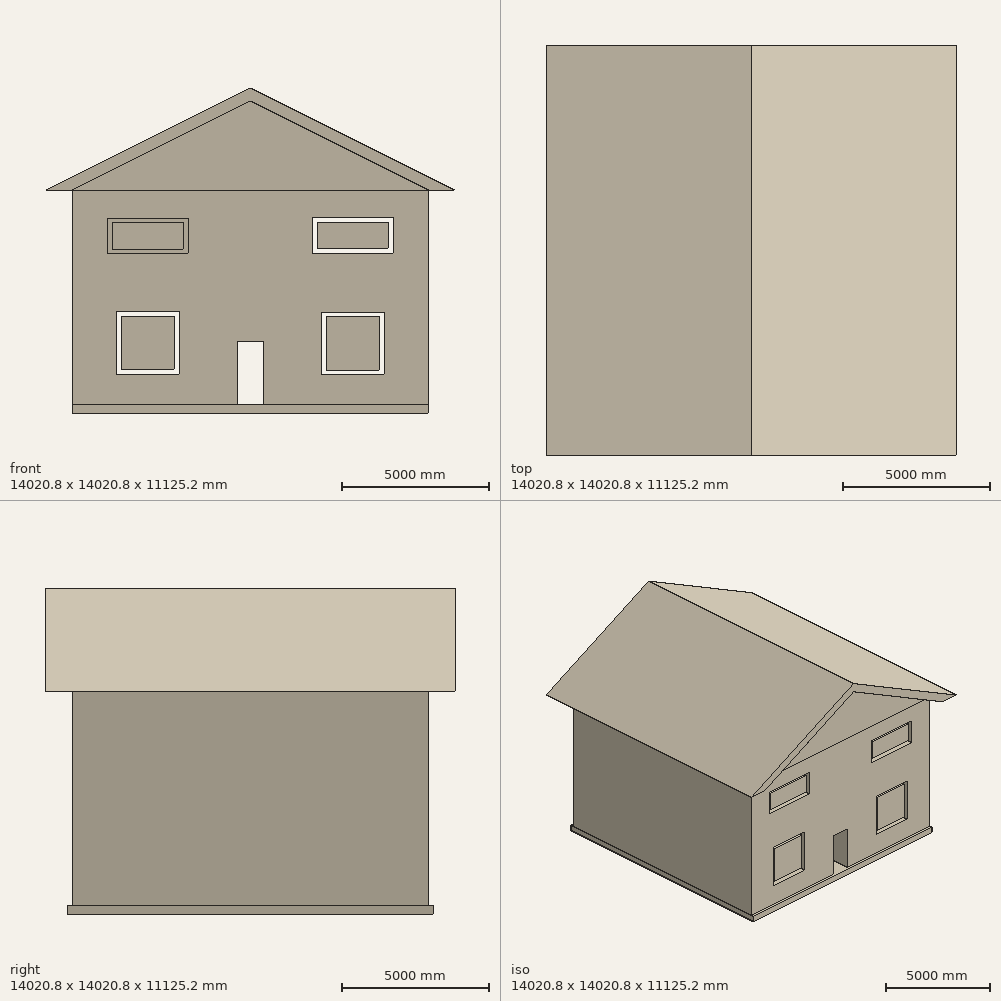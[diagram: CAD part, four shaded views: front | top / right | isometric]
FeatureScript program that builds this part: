
annotation { "Feature Type Name" : "Feature", "Feature Type Description" : "" }
export const myFeature = defineFeature(function(context is Context, id is Id, definition is map)
    precondition{}
    {
        {
            var Q0;
            Q0=qCreatedBy(makeId("Front.planeOp"),FACE);
            var sketch = newSketch(context, id + "F0", { "sketchPlane" : qUnion([Q0])});
            skLineSegment(sketch, "E0", {"start": v(0, 0) * mm, "end": v(-6096, 0) * mm});
            skLineSegment(sketch, "E1", {"start": v(0, 0) * mm, "end": v(6096, 0) * mm});
            skLineSegment(sketch, "E2", {"start": v(0, 0) * mm, "end": v(0, 3048) * mm, "construction": true});
            skLineSegment(sketch, "E3", {"start": v(-6096, 0) * mm, "end": v(0, 3048) * mm});
            skLineSegment(sketch, "E4", {"start": v(0, 3048) * mm, "end": v(6096, 0) * mm});
            skLineSegment(sketch, "E5", {"start": v(-6096, 0) * mm, "end": v(-7010.4, 0) * mm});
            skLineSegment(sketch, "E6", {"start": v(6096, 0) * mm, "end": v(7010.4, 0) * mm});
            skLineSegment(sketch, "E7", {"start": v(0, 3048) * mm, "end": v(0, 3505.2) * mm});
            skLineSegment(sketch, "E8", {"start": v(0, 3505.2) * mm, "end": v(7010.4, 0) * mm});
            skLineSegment(sketch, "E9", {"start": v(-7010.4, 0) * mm, "end": v(0, 3505.2) * mm});
            skLineSegment(sketch, "E10", {"start": v(-6096, 0) * mm, "end": v(-6096, -7315.2) * mm});
            skLineSegment(sketch, "E11", {"start": v(6096, 0) * mm, "end": v(6096, -7315.2) * mm});
            skLineSegment(sketch, "E12", {"start": v(-6096, -7315.2) * mm, "end": v(6096, -7315.2) * mm});
            skLineSegment(sketch, "E13", {"start": v(-6096, -7315.2) * mm, "end": v(-6096, -7620) * mm});
            skLineSegment(sketch, "E14", {"start": v(-6096, -7620) * mm, "end": v(6096, -7620) * mm});
            skLineSegment(sketch, "E15", {"start": v(6096, -7620) * mm, "end": v(6096, -7315.2) * mm});
            skLineSegment(sketch, "E16", {"start": v(0, 0) * mm, "end": v(0, -7315.2) * mm, "construction": true});
            skLineSegment(sketch, "E17", {"start": v(0, -7315.2) * mm, "end": v(-457.2, -7315.2) * mm});
            skLineSegment(sketch, "E18", {"start": v(-457.2, -7315.2) * mm, "end": v(-457.2, -5181.6) * mm});
            skLineSegment(sketch, "E19", {"start": v(-457.2, -5181.6) * mm, "end": v(457.2, -5181.6) * mm});
            skLineSegment(sketch, "E20", {"start": v(457.2, -5181.6) * mm, "end": v(457.2, -7315.2) * mm});
            skLineSegment(sketch, "E21", {"start": v(457.2, -7315.2) * mm, "end": v(0, -7315.2) * mm});
            skLineSegment(sketch, "E22.bottom", {"start": v(2438.4, -4174.44) * mm, "end": v(4572, -4174.44) * mm});
            skLineSegment(sketch, "E22.top", {"start": v(2438.4, -6308.04) * mm, "end": v(4572, -6308.04) * mm});
            skLineSegment(sketch, "E22.left", {"start": v(2438.4, -4174.44) * mm, "end": v(2438.4, -6308.04) * mm});
            skLineSegment(sketch, "E22.right", {"start": v(4572, -4174.44) * mm, "end": v(4572, -6308.04) * mm});
            skLineSegment(sketch, "E23.bottom", {"start": v(-4572, -4154.53) * mm, "end": v(-2438.4, -4154.53) * mm});
            skLineSegment(sketch, "E23.top", {"start": v(-4572, -6288.13) * mm, "end": v(-2438.4, -6288.13) * mm});
            skLineSegment(sketch, "E23.left", {"start": v(-4572, -4154.53) * mm, "end": v(-4572, -6288.13) * mm});
            skLineSegment(sketch, "E23.right", {"start": v(-2438.4, -4154.53) * mm, "end": v(-2438.4, -6288.13) * mm});
            skLineSegment(sketch, "E24.bottom", {"start": v(-4876.8, -947.78) * mm, "end": v(-2133.6, -947.78) * mm});
            skLineSegment(sketch, "E24.top", {"start": v(-4876.8, -2166.98) * mm, "end": v(-2133.6, -2166.98) * mm});
            skLineSegment(sketch, "E24.left", {"start": v(-4876.8, -947.78) * mm, "end": v(-4876.8, -2166.98) * mm});
            skLineSegment(sketch, "E24.right", {"start": v(-2133.6, -947.78) * mm, "end": v(-2133.6, -2166.98) * mm});
            skLineSegment(sketch, "E25.bottom", {"start": v(2133.6, -937.76) * mm, "end": v(4876.8, -937.76) * mm});
            skLineSegment(sketch, "E25.top", {"start": v(2133.6, -2156.96) * mm, "end": v(4876.8, -2156.96) * mm});
            skLineSegment(sketch, "E25.left", {"start": v(2133.6, -937.76) * mm, "end": v(2133.6, -2156.96) * mm});
            skLineSegment(sketch, "E25.right", {"start": v(4876.8, -937.76) * mm, "end": v(4876.8, -2156.96) * mm});
            skLineSegment(sketch, "E26.0", {"start": v(2590.8, -6155.64) * mm, "end": v(4419.6, -6155.64) * mm});
            skLineSegment(sketch, "E26.1", {"start": v(2590.8, -4326.84) * mm, "end": v(2590.8, -6155.64) * mm});
            skLineSegment(sketch, "E26.2", {"start": v(2590.8, -4326.84) * mm, "end": v(4419.6, -4326.84) * mm});
            skLineSegment(sketch, "E26.3", {"start": v(4419.6, -4326.84) * mm, "end": v(4419.6, -6155.64) * mm});
            skLineSegment(sketch, "E27.0", {"start": v(4567, -4179.44) * mm, "end": v(4567, -6308.04) * mm});
            skLineSegment(sketch, "E27.1", {"start": v(2443.4, -4179.44) * mm, "end": v(4567, -4179.44) * mm});
            skLineSegment(sketch, "E27.2", {"start": v(2443.4, -4179.44) * mm, "end": v(2443.4, -6308.04) * mm});
            skLineSegment(sketch, "E28.0", {"start": v(-4419.6, -4306.93) * mm, "end": v(-2590.8, -4306.93) * mm});
            skLineSegment(sketch, "E28.1", {"start": v(-4419.6, -4306.93) * mm, "end": v(-4419.6, -6135.73) * mm});
            skLineSegment(sketch, "E28.2", {"start": v(-4419.6, -6135.73) * mm, "end": v(-2590.8, -6135.73) * mm});
            skLineSegment(sketch, "E28.3", {"start": v(-2590.8, -4306.93) * mm, "end": v(-2590.8, -6135.73) * mm});
            skLineSegment(sketch, "E29.0", {"start": v(-4724.4, -1100.18) * mm, "end": v(-2286, -1100.18) * mm});
            skLineSegment(sketch, "E29.1", {"start": v(-4724.4, -1100.18) * mm, "end": v(-4724.4, -2014.58) * mm});
            skLineSegment(sketch, "E29.2", {"start": v(-4724.4, -2014.58) * mm, "end": v(-2286, -2014.58) * mm});
            skLineSegment(sketch, "E29.3", {"start": v(-2286, -1100.18) * mm, "end": v(-2286, -2014.58) * mm});
            skLineSegment(sketch, "E30.0", {"start": v(2286, -1090.16) * mm, "end": v(4724.4, -1090.16) * mm});
            skLineSegment(sketch, "E30.1", {"start": v(2286, -1090.16) * mm, "end": v(2286, -2004.56) * mm});
            skLineSegment(sketch, "E30.2", {"start": v(2286, -2004.56) * mm, "end": v(4724.4, -2004.56) * mm});
            skLineSegment(sketch, "E30.3", {"start": v(4724.4, -1090.16) * mm, "end": v(4724.4, -2004.56) * mm});
            skSolve(sketch);
        }
        {
            var Q0;
            Q0=makeQuery(id+"F0.imprint","IMPRINT",FACE,{"disambiguationData":[TD([[makeQuery(id+"F0.imprint","IMPRINT",EDGE,{"derivedFrom":sQuery(id+"F0.wireOp",EDGE,"E4")}),1.0]])]});
            var Q1;
            Q1=makeQuery(id+"F0.imprint","IMPRINT",FACE,{"disambiguationData":[TD([[makeQuery(id+"F0.imprint","IMPRINT",EDGE,{"derivedFrom":sQuery(id+"F0.wireOp",EDGE,"E3")}),1.0]])]});
            extrude(context, id + "F1", {"entities" : qUnion([Q0, Q1]), "endBound" : BoundingType.SYMMETRIC, "depth" : 14020.8 * mm, "offsetDistance" : 30.48 * mm});
        }
        {
            var Q0;
            Q0=makeQuery(id+"F0.imprint","IMPRINT",FACE,{"disambiguationData":[TD([[makeQuery(id+"F0.imprint","IMPRINT",EDGE,{"derivedFrom":sQuery(id+"F0.wireOp",EDGE,"E0")}),-1.0]])]});
            extrude(context, id + "F2", {"entities" : qUnion([Q0]), "operationType" : NewBodyOperationType.ADD, "endBound" : BoundingType.SYMMETRIC, "depth" : 12496.8 * mm, "offsetDistance" : 30.48 * mm});
        }
        {
            var Q0;
            {var subQ0=sQuery(id+"F0.wireOp",EDGE,"E13");Q0=makeQuery(id+"F0.imprint","IMPRINT",FACE,{"disambiguationData":[TD([[makeQuery(id+"F0.imprint","IMPRINT",EDGE,{"derivedFrom":subQ0}),1.0]])]});}
            extrude(context, id + "F3", {"entities" : qUnion([Q0]), "endBound" : BoundingType.SYMMETRIC, "depth" : 12496.8 * mm, "offsetDistance" : 30.48 * mm});
        }
        {
            var Q0;
            Q0=makeQuery(id+"F0.imprint","IMPRINT",FACE,{"disambiguationData":[TD([[makeQuery(id+"F0.imprint","IMPRINT",EDGE,{"derivedFrom":sQuery(id+"F0.wireOp",EDGE,"E0")}),1.0]])]});
            extrude(context, id + "F4", {"entities" : qUnion([Q0]), "endBound" : BoundingType.SYMMETRIC, "depth" : 12192 * mm, "offsetDistance" : 30.48 * mm});
        }
        {
            var Q0;
            Q0=makeQuery(id+"F0.imprint","IMPRINT",FACE,{"disambiguationData":[TD([[makeQuery(id+"F0.imprint","IMPRINT",EDGE,{"derivedFrom":sQuery(id+"F0.wireOp",EDGE,"E26.0")}),1.0]])]});
            var Q1;
            Q1=makeQuery(id+"F0.imprint","IMPRINT",FACE,{"disambiguationData":[TD([[makeQuery(id+"F0.imprint","IMPRINT",EDGE,{"derivedFrom":sQuery(id+"F0.wireOp",EDGE,"E30.0")}),-1.0]])]});
            var Q2;
            Q2=makeQuery(id+"F0.imprint","IMPRINT",FACE,{"disambiguationData":[TD([[makeQuery(id+"F0.imprint","IMPRINT",EDGE,{"derivedFrom":sQuery(id+"F0.wireOp",EDGE,"E29.0")}),-1.0]])]});
            var Q3;
            Q3=makeQuery(id+"F0.imprint","IMPRINT",FACE,{"disambiguationData":[TD([[makeQuery(id+"F0.imprint","IMPRINT",EDGE,{"derivedFrom":sQuery(id+"F0.wireOp",EDGE,"E28.0")}),-1.0]])]});
            var Q4;
            Q4=makeQuery(id+"F0.imprint","IMPRINT",FACE,{"disambiguationData":[TD([[makeQuery(id+"F0.imprint","IMPRINT",EDGE,{"derivedFrom":sQuery(id+"F0.wireOp",EDGE,"E17")}),-1.0]])]});
            extrude(context, id + "F5", {"entities" : qUnion([Q0, Q1, Q2, Q3, Q4]), "endBound" : BoundingType.SYMMETRIC, "depth" : 12039.6 * mm, "offsetDistance" : 30.48 * mm});
        }
        {
            var Q0;
            Q0=makeQuery(id+"F0.imprint","IMPRINT",FACE,{"disambiguationData":[TD([[makeQuery(id+"F0.imprint","IMPRINT",EDGE,{"derivedFrom":sQuery(id+"F0.wireOp",EDGE,"E24.bottom")}),-1.0]])]});
            extrude(context, id + "F6", {"entities" : qUnion([Q0]), "endBound" : BoundingType.SYMMETRIC, "depth" : 152.4 * mm, "offsetDistance" : 30.48 * mm});
        }
    });
